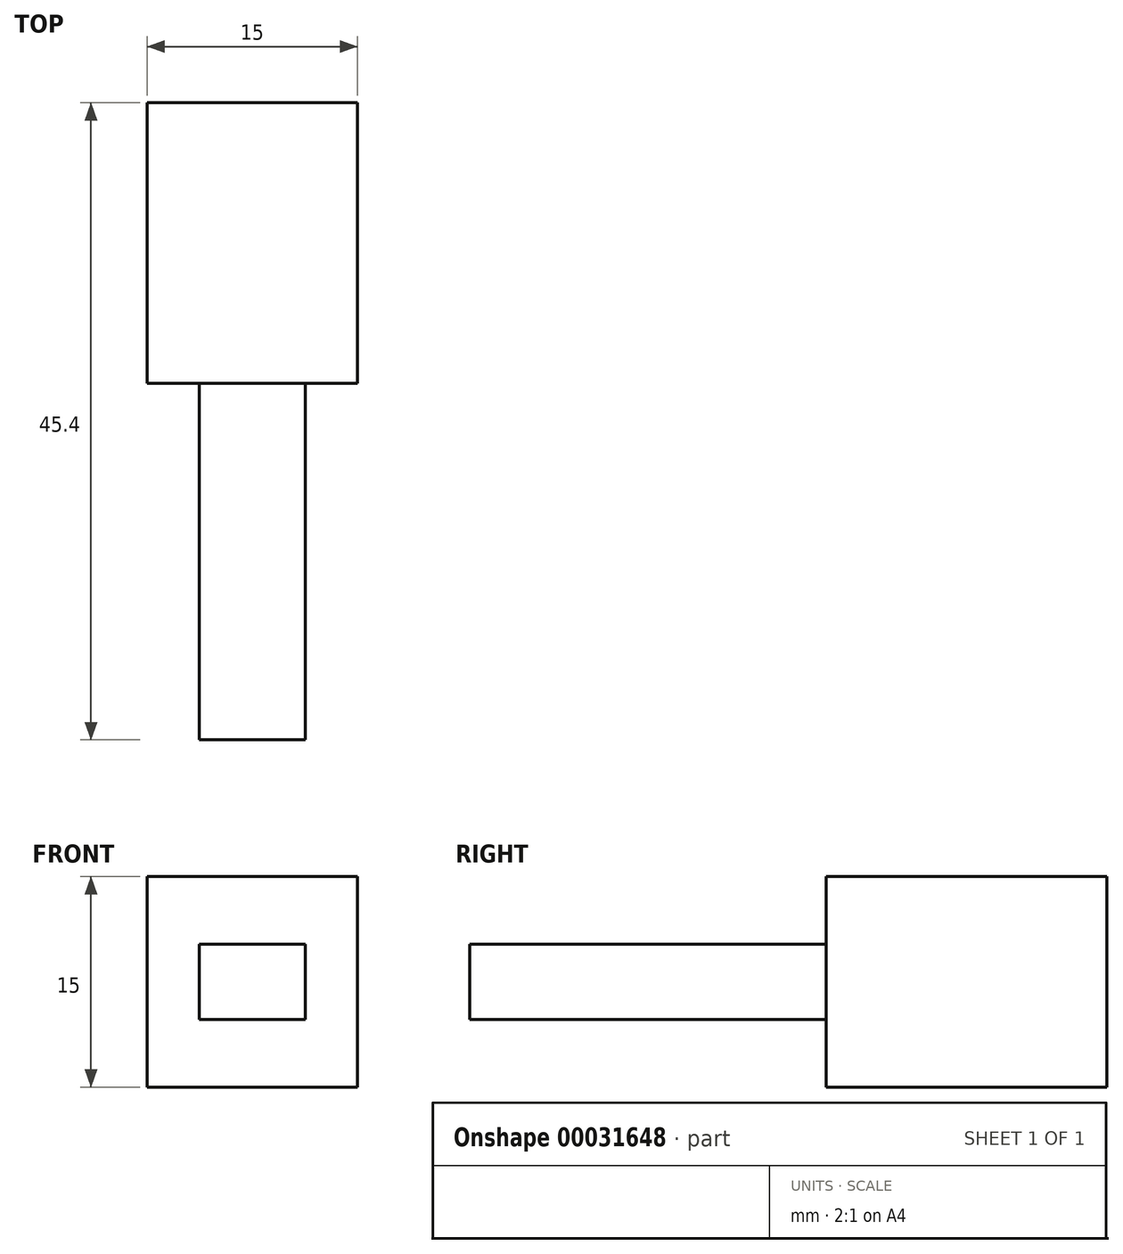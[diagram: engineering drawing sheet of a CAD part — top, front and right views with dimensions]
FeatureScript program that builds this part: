
annotation { "Feature Type Name" : "Feature", "Feature Type Description" : "" }
export const myFeature = defineFeature(function(context is Context, id is Id, definition is map)
    precondition{}
    {
        {
            var Q0;
            Q0=qCreatedBy(makeId("Front.planeOp"),FACE);
            var sketch = newSketch(context, id + "F0", { "sketchPlane" : qUnion([Q0])});
            skLineSegment(sketch, "E0.rect.bottom", {"start": v(-7.5, 7.5) * mm, "end": v(7.5, 7.5) * mm});
            skLineSegment(sketch, "E0.rect.top", {"start": v(-7.5, -7.5) * mm, "end": v(7.5, -7.5) * mm});
            skLineSegment(sketch, "E0.rect.left", {"start": v(-7.5, 7.5) * mm, "end": v(-7.5, -7.5) * mm});
            skLineSegment(sketch, "E0.rect.right", {"start": v(7.5, 7.5) * mm, "end": v(7.5, -7.5) * mm});
            skPoint(sketch, "E0.rect.middle", {"position": v(0, 0) * mm});
            skSolve(sketch);
        }
        {
            var Q0;
            Q0 = qSketchRegion(id + "F0", true);
            extrude(context, id + "F1", {"entities" : qUnion([Q0]), "endBound" : BoundingType.SYMMETRIC, "depth" : 20 * mm});
        }
        {
            var Q0;
            Q0=makeQuery(id+"F1.opExtrude","CAP_FACE",FACE,{"disambiguationData":[OSD([sQuery(id+"F0.wireOp",EDGE,"E0.rect.bottom"),sQuery(id+"F0.wireOp",EDGE,"E0.rect.top"),sQuery(id+"F0.wireOp",EDGE,"E0.rect.left"),sQuery(id+"F0.wireOp",EDGE,"E0.rect.right")])],"isStart":false});
            var sketch = newSketch(context, id + "F2", { "sketchPlane" : qUnion([Q0])});
            skLineSegment(sketch, "E1.rect.bottom", {"start": v(-3.79, 2.68) * mm, "end": v(3.79, 2.68) * mm});
            skLineSegment(sketch, "E1.rect.top", {"start": v(-3.79, -2.68) * mm, "end": v(3.79, -2.68) * mm});
            skLineSegment(sketch, "E1.rect.left", {"start": v(-3.79, 2.68) * mm, "end": v(-3.79, -2.68) * mm});
            skLineSegment(sketch, "E1.rect.right", {"start": v(3.79, 2.68) * mm, "end": v(3.79, -2.68) * mm});
            skPoint(sketch, "E1.rect.middle", {"position": v(0, 0) * mm});
            skSolve(sketch);
        }
        {
            var Q0;
            Q0=makeQuery(id+"F2.imprint","IMPRINT",FACE,{"disambiguationData":[TD([[makeQuery(id+"F2.imprint","IMPRINT",EDGE,{"derivedFrom":sQuery(id+"F2.wireOp",EDGE,"E1.rect.bottom")}),-1.0]])]});
            extrude(context, id + "F3", {"entities" : qUnion([Q0]), "operationType" : NewBodyOperationType.ADD, "depth" : 25.4 * mm});
        }
    });
